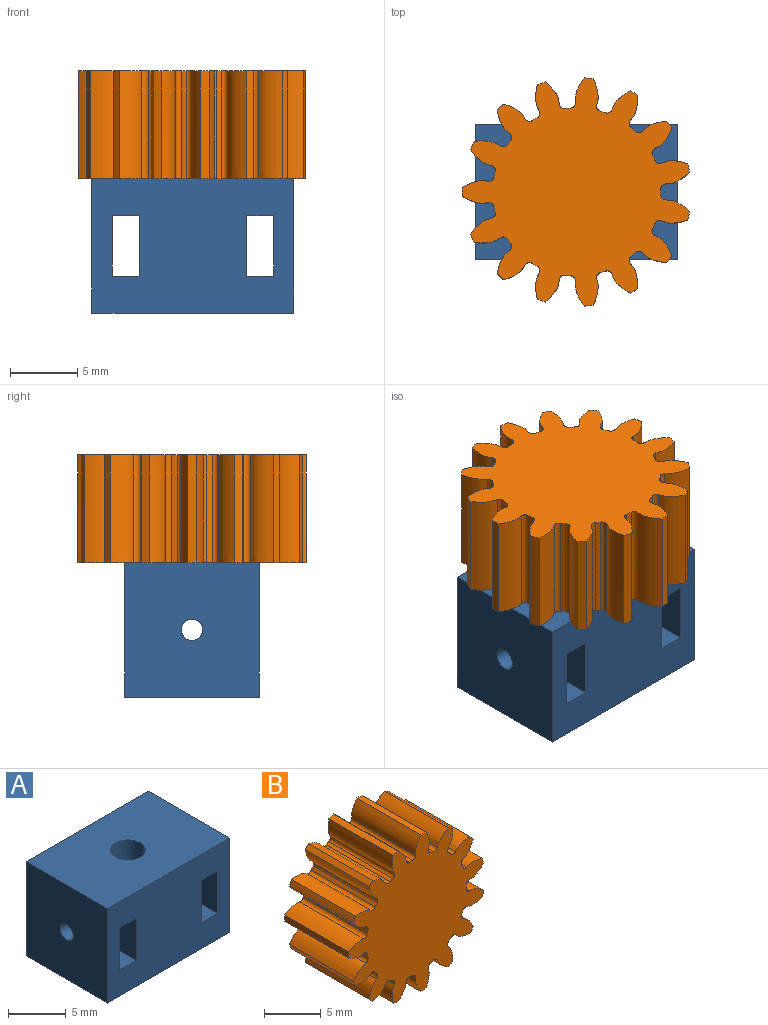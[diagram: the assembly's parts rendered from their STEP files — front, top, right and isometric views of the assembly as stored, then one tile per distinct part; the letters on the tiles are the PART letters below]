
ASSEMBLY  parts=2 mates=1
PART A: 19 faces, bbox 15x10x10 mm
  f0: plane 10x10mm, normal (1,0,0), area 98mm2, adj f1,f3,f4,f5,f18
  f1: plane 15x10mm, normal (0,1,0), area 132mm2, adj f0,f2,f4,f5,f6,f7,f8,f9
  f2: plane 10x10mm, normal (-1,0,0), area 98mm2, adj f1,f3,f4,f5,f17
  f3: plane 15x10mm, normal (0,-1,0), area 132mm2, adj f0,f2,f4,f5,f6,f7,f8,f9
  f4: plane 15x10mm, normal (0,0,1), area 142.9mm2, adj f0,f1,f2,f3,f14
  f5: plane 15x10mm, normal (0,0,-1), area 142.9mm2, adj f0,f1,f2,f3,f14
  f6: plane 10x2mm, normal (0,0,-1), area 20mm2, adj f1,f3,f7,f8
  f7: plane 10x4.5mm, normal (-1,0,0), area 43mm2, adj f1,f3,f6,f9,f18
  f8: plane 10x4.5mm, normal (1,0,0), area 43mm2, adj f1,f3,f6,f9,f15
  f9: plane 10x2mm, normal (0,0,1), area 20mm2, adj f1,f3,f7,f8
  f10: plane 10x2mm, normal (0,0,1), area 20mm2, adj f1,f3,f11,f12
  f11: plane 10x4.5mm, normal (1,0,0), area 43mm2, adj f1,f3,f10,f13,f17
  f12: plane 10x4.5mm, normal (-1,0,0), area 43mm2, adj f1,f3,f10,f13,f16
  f13: plane 10x2mm, normal (0,0,-1), area 20mm2, adj f1,f3,f11,f12
  f14: cylinder r=1.5mm len=10mm, axis (0,0,-1), area 90.1mm2, adj f4,f5,f15,f16
  f15: cylinder r=0.8mm len=2.73mm, axis (-1,0,0), area 13.1mm2, adj f8,f14
  f16: cylinder r=0.8mm len=2.73mm, axis (-1,0,0), area 13.1mm2, adj f12,f14
  f17: cylinder r=0.8mm len=1.6mm, axis (-1,0,0), area 7.5mm2, adj f2,f11
  f18: cylinder r=0.8mm len=1.6mm, axis (-1,0,0), area 7.5mm2, adj f0,f7
PART B: 92 faces, bbox 16.9x8x17 mm
  f0: extruded ~8x1.79mm, area 16.3mm2, adj f59,f60,f61,f62
  f1: cylinder r=6.25mm len=8mm, axis (0,1,0), area 3.3mm2, adj f60,f61,f62,f63
  f2: extruded ~8x1.79mm, area 16.3mm2, adj f3,f60,f61,f63
  f3: cylinder r=8.5mm len=8mm, axis (0,1,0), area 5.2mm2, adj f2,f4,f60,f61
  f4: extruded ~8x1.98mm, area 16.3mm2, adj f3,f60,f61,f64
  f5: cylinder r=6.25mm len=8mm, axis (0,1,0), area 3.3mm2, adj f60,f61,f64,f65
  f6: extruded ~8x1.51mm, area 16.3mm2, adj f7,f60,f61,f65
  f7: cylinder r=8.5mm len=8mm, axis (0,1,0), area 5.2mm2, adj f6,f8,f60,f61
  f8: extruded ~8x1.83mm, area 16.3mm2, adj f7,f60,f61,f66
  f9: cylinder r=6.25mm len=8mm, axis (0,1,0), area 3.3mm2, adj f60,f61,f66,f67
  f10: extruded ~8x1.9mm, area 16.3mm2, adj f11,f60,f61,f67
  f11: cylinder r=8.5mm len=8mm, axis (0,1,0), area 5.2mm2, adj f10,f12,f60,f61
  f12: extruded ~8x1.44mm, area 16.3mm2, adj f11,f60,f61,f68
  f13: cylinder r=6.25mm len=8mm, axis (0,1,0), area 3.3mm2, adj f60,f61,f68,f69
  f14: extruded ~8x1.97mm, area 16.3mm2, adj f15,f60,f61,f69
  f15: cylinder r=8.5mm len=8mm, axis (0,1,0), area 5.2mm2, adj f14,f16,f60,f61
  f16: extruded ~8x1.87mm, area 16.3mm2, adj f15,f60,f61,f70
  f17: cylinder r=6.25mm len=8mm, axis (0,1,0), area 3.3mm2, adj f60,f61,f70,f71
  f18: extruded ~8x1.69mm, area 16.3mm2, adj f19,f60,f61,f71
  f19: cylinder r=8.5mm len=8mm, axis (0,1,0), area 5.2mm2, adj f18,f20,f60,f61
  f20: extruded ~8x1.98mm, area 16.3mm2, adj f19,f60,f61,f72
  f21: cylinder r=6.25mm len=8mm, axis (0,1,0), area 3.3mm2, adj f60,f61,f72,f73
  f22: extruded ~8x1.63mm, area 16.3mm2, adj f23,f60,f61,f73
  f23: cylinder r=8.5mm len=8mm, axis (0,1,0), area 5.2mm2, adj f22,f24,f60,f61
  f24: extruded ~8x1.74mm, area 16.3mm2, adj f23,f60,f61,f74
  f25: cylinder r=6.25mm len=8mm, axis (0,1,0), area 3.3mm2, adj f60,f61,f74,f75
  f26: extruded ~8x1.95mm, area 16.3mm2, adj f27,f60,f61,f75
  f27: cylinder r=8.5mm len=8mm, axis (0,1,0), area 5.2mm2, adj f26,f28,f60,f61
  f28: extruded ~8x1.57mm, area 16.3mm2, adj f27,f60,f61,f76
  f29: cylinder r=6.25mm len=8mm, axis (0,1,0), area 3.3mm2, adj f60,f61,f76,f77
  f30: extruded ~8x1.93mm, area 16.3mm2, adj f31,f60,f61,f77
  f31: cylinder r=8.5mm len=8mm, axis (0,1,0), area 5.2mm2, adj f30,f32,f60,f61
  f32: extruded ~8x1.93mm, area 16.3mm2, adj f31,f60,f61,f78
  f33: cylinder r=6.25mm len=8mm, axis (0,1,0), area 3.3mm2, adj f60,f61,f78,f79
  f34: extruded ~8x1.57mm, area 16.3mm2, adj f35,f60,f61,f79
  f35: cylinder r=8.5mm len=8mm, axis (0,1,0), area 5.2mm2, adj f34,f36,f60,f61
  f36: extruded ~8x1.95mm, area 16.3mm2, adj f35,f60,f61,f80
  f37: cylinder r=6.25mm len=8mm, axis (0,1,0), area 3.3mm2, adj f60,f61,f80,f81
  f38: extruded ~8x1.74mm, area 16.3mm2, adj f39,f60,f61,f81
  f39: cylinder r=8.5mm len=8mm, axis (0,1,0), area 5.2mm2, adj f38,f40,f60,f61
  f40: extruded ~8x1.63mm, area 16.3mm2, adj f39,f60,f61,f82
  f41: cylinder r=6.25mm len=8mm, axis (0,1,0), area 3.3mm2, adj f60,f61,f82,f83
  f42: extruded ~8x1.98mm, area 16.3mm2, adj f43,f60,f61,f83
  f43: cylinder r=8.5mm len=8mm, axis (0,1,0), area 5.2mm2, adj f42,f44,f60,f61
  f44: extruded ~8x1.69mm, area 16.3mm2, adj f43,f60,f61,f84
  f45: cylinder r=6.25mm len=8mm, axis (0,1,0), area 3.3mm2, adj f60,f61,f84,f85
  f46: extruded ~8x1.87mm, area 16.3mm2, adj f47,f60,f61,f85
  f47: cylinder r=8.5mm len=8mm, axis (0,1,0), area 5.2mm2, adj f46,f48,f60,f61
  f48: extruded ~8x1.97mm, area 16.3mm2, adj f47,f60,f61,f86
  f49: cylinder r=6.25mm len=8mm, axis (0,1,0), area 3.3mm2, adj f60,f61,f86,f87
  f50: extruded ~8x1.44mm, area 16.3mm2, adj f51,f60,f61,f87
  f51: cylinder r=8.5mm len=8mm, axis (0,1,0), area 5.2mm2, adj f50,f52,f60,f61
  f52: extruded ~8x1.9mm, area 16.3mm2, adj f51,f60,f61,f88
  f53: cylinder r=6.25mm len=8mm, axis (0,1,0), area 3.3mm2, adj f60,f61,f88,f89
  f54: extruded ~8x1.83mm, area 16.3mm2, adj f55,f60,f61,f89
  f55: cylinder r=8.5mm len=8mm, axis (0,1,0), area 5.2mm2, adj f54,f56,f60,f61
  f56: extruded ~8x1.51mm, area 16.3mm2, adj f55,f60,f61,f90
  f57: cylinder r=6.25mm len=8mm, axis (0,1,0), area 3.3mm2, adj f60,f61,f90,f91
  f58: extruded ~8x1.98mm, area 16.3mm2, adj f59,f60,f61,f91
  f59: cylinder r=8.5mm len=8mm, axis (0,1,0), area 5.2mm2, adj f0,f58,f60,f61
  f60: plane 16.99x16.9mm, normal (0,-1,0), area 171.4mm2, adj f0,f1,f2,f3,f4,f5,f6,f7
  f61: plane 16.99x16.9mm, normal (0,1,0), area 171.4mm2, adj f0,f1,f2,f3,f4,f5,f6,f7
  f62: cylinder r=0.37mm len=8mm, axis (0,1,0), area 4.5mm2, adj f0,f1,f60,f61
  f63: cylinder r=0.37mm len=8mm, axis (0,1,0), area 4.5mm2, adj f1,f2,f60,f61
  f64: cylinder r=0.37mm len=8mm, axis (0,1,0), area 4.5mm2, adj f4,f5,f60,f61
  f65: cylinder r=0.37mm len=8mm, axis (0,1,0), area 4.5mm2, adj f5,f6,f60,f61
  f66: cylinder r=0.37mm len=8mm, axis (0,1,0), area 4.5mm2, adj f8,f9,f60,f61
  f67: cylinder r=0.37mm len=8mm, axis (0,1,0), area 4.5mm2, adj f9,f10,f60,f61
  f68: cylinder r=0.37mm len=8mm, axis (0,1,0), area 4.5mm2, adj f12,f13,f60,f61
  f69: cylinder r=0.37mm len=8mm, axis (0,1,0), area 4.5mm2, adj f13,f14,f60,f61
  f70: cylinder r=0.37mm len=8mm, axis (0,1,0), area 4.5mm2, adj f16,f17,f60,f61
  f71: cylinder r=0.37mm len=8mm, axis (0,1,0), area 4.5mm2, adj f17,f18,f60,f61
  f72: cylinder r=0.37mm len=8mm, axis (0,1,0), area 4.5mm2, adj f20,f21,f60,f61
  f73: cylinder r=0.37mm len=8mm, axis (0,1,0), area 4.5mm2, adj f21,f22,f60,f61
  f74: cylinder r=0.37mm len=8mm, axis (0,1,0), area 4.5mm2, adj f24,f25,f60,f61
  f75: cylinder r=0.37mm len=8mm, axis (0,1,0), area 4.5mm2, adj f25,f26,f60,f61
  f76: cylinder r=0.37mm len=8mm, axis (0,1,0), area 4.5mm2, adj f28,f29,f60,f61
  f77: cylinder r=0.37mm len=8mm, axis (0,1,0), area 4.5mm2, adj f29,f30,f60,f61
  f78: cylinder r=0.37mm len=8mm, axis (0,1,0), area 4.5mm2, adj f32,f33,f60,f61
  f79: cylinder r=0.37mm len=8mm, axis (0,1,0), area 4.5mm2, adj f33,f34,f60,f61
  f80: cylinder r=0.37mm len=8mm, axis (0,1,0), area 4.5mm2, adj f36,f37,f60,f61
  f81: cylinder r=0.37mm len=8mm, axis (0,1,0), area 4.5mm2, adj f37,f38,f60,f61
  f82: cylinder r=0.37mm len=8mm, axis (0,1,0), area 4.5mm2, adj f40,f41,f60,f61
  f83: cylinder r=0.37mm len=8mm, axis (0,1,0), area 4.5mm2, adj f41,f42,f60,f61
  f84: cylinder r=0.37mm len=8mm, axis (0,1,0), area 4.5mm2, adj f44,f45,f60,f61
  f85: cylinder r=0.37mm len=8mm, axis (0,1,0), area 4.5mm2, adj f45,f46,f60,f61
  f86: cylinder r=0.37mm len=8mm, axis (0,1,0), area 4.5mm2, adj f48,f49,f60,f61
  f87: cylinder r=0.37mm len=8mm, axis (0,1,0), area 4.5mm2, adj f49,f50,f60,f61
  f88: cylinder r=0.37mm len=8mm, axis (0,1,0), area 4.5mm2, adj f52,f53,f60,f61
  f89: cylinder r=0.37mm len=8mm, axis (0,1,0), area 4.5mm2, adj f53,f54,f60,f61
  f90: cylinder r=0.37mm len=8mm, axis (0,1,0), area 4.5mm2, adj f56,f57,f60,f61
  f91: cylinder r=0.37mm len=8mm, axis (0,1,0), area 4.5mm2, adj f57,f58,f60,f61
PLACE A t=(0,0,-3)mm
PLACE B rot(axis=(1,0,0),90deg) t=(0,0,15)mm
MATE fastened B.f3 <-> A.f14  axis (0,0,-1) through (0,0,7)mm
